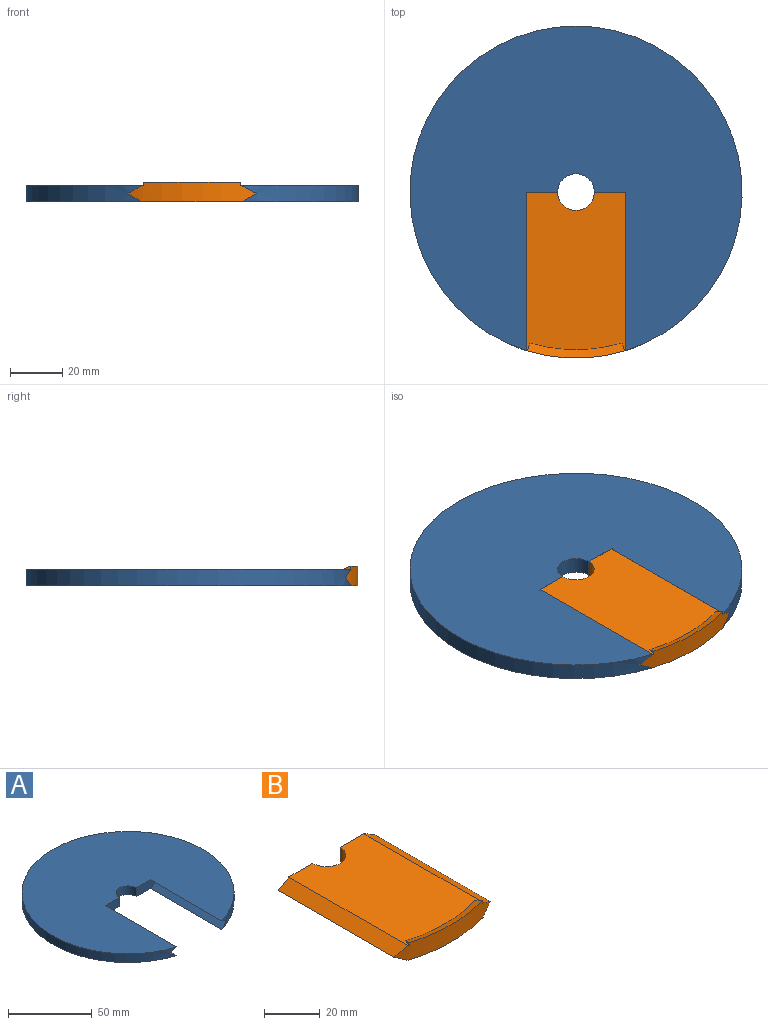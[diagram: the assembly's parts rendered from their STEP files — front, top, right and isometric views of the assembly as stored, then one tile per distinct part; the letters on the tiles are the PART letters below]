
ASSEMBLY  parts=2 mates=1
PART A: 10 faces, bbox 127x124.1x6.4 mm
  f0: cylinder r=63.5mm len=127mm, axis (0,0,-1), area 2250.8mm2, adj f4,f5,f6,f7,f8,f9
  f1: cylinder r=7mm len=14mm, axis (0,0,-1), area 139.6mm2, adj f2,f3,f4,f5
  f2: plane 17.55x6.35mm, normal (0,-1,0), area 94mm2, adj f1,f4,f5,f8,f9
  f3: plane 17.55x6.35mm, normal (0,-1,0), area 94mm2, adj f1,f4,f5,f6,f7
  f4: plane 127x124.08mm, normal (0,0,1), area 10208.2mm2, adj f0,f1,f2,f3,f6,f9
  f5: plane 127x124.08mm, normal (0,0,-1), area 10208.2mm2, adj f0,f1,f2,f3,f7,f8
  f6: plane 60.58x5.5mm, normal (0.5,0,-0.87), area 378.6mm2, adj f0,f3,f4,f7
  f7: plane 60.58x5.5mm, normal (0.5,0,0.87), area 378.6mm2, adj f0,f3,f5,f6
  f8: plane 60.58x5.5mm, normal (-0.5,0,0.87), area 378.6mm2, adj f0,f2,f5,f9
  f9: plane 60.58x5.5mm, normal (-0.5,0,-0.87), area 378.6mm2, adj f0,f2,f4,f8
PART B: 13 faces, bbox 49x63.5x7.6 mm
  f0: plane 60.73x38.04mm, normal (0,0,1), area 2185.3mm2, adj f1,f2,f4,f5,f6,f8,f10,f11
  f1: plane 17.52x6.35mm, normal (0,1,0), area 93.8mm2, adj f0,f3,f5,f8,f9
  f2: cylinder r=63.5mm len=49.04mm, axis (0,0,-1), area 330.2mm2, adj f0,f3,f6,f7,f8,f9,f10,f11
  f3: plane 63.5x38.04mm, normal (0,0,-1), area 2301.9mm2, adj f1,f2,f4,f5,f7,f9
  f4: plane 17.52x6.35mm, normal (0,1,0), area 93.8mm2, adj f0,f3,f5,f6,f7
  f5: cylinder r=7mm len=14mm, axis (0,0,-1), area 139.6mm2, adj f0,f1,f3,f4
  f6: plane 60.58x5.5mm, normal (-0.5,0,0.87), area 378.6mm2, adj f0,f2,f4,f7
  f7: plane 60.58x5.5mm, normal (-0.5,0,-0.87), area 378.6mm2, adj f2,f3,f4,f6
  f8: plane 60.58x5.5mm, normal (0.5,0,0.87), area 378.6mm2, adj f0,f1,f2,f9
  f9: plane 60.58x5.5mm, normal (0.5,0,-0.87), area 378.6mm2, adj f1,f2,f3,f8
  f10: cone r=63.5mm half-angle=68.2deg, axis (0,0,1), area 125.6mm2, adj f0,f2,f11,f12
  f11: plane 3.04x1.27mm, normal (-0.96,0.29,0), area 2mm2, adj f0,f2,f10
  f12: plane 3.04x1.27mm, normal (0.96,0.29,0), area 2mm2, adj f0,f2,f10
PLACE A t=(-37.38,-32.6,-16.82)mm
PLACE B t=(-37.39,-32.6,-16.82)mm
MATE slider A.f3 <-> B.f4  axis (0,-1,0) through (-51.86,-32.6,-13.65)mm
